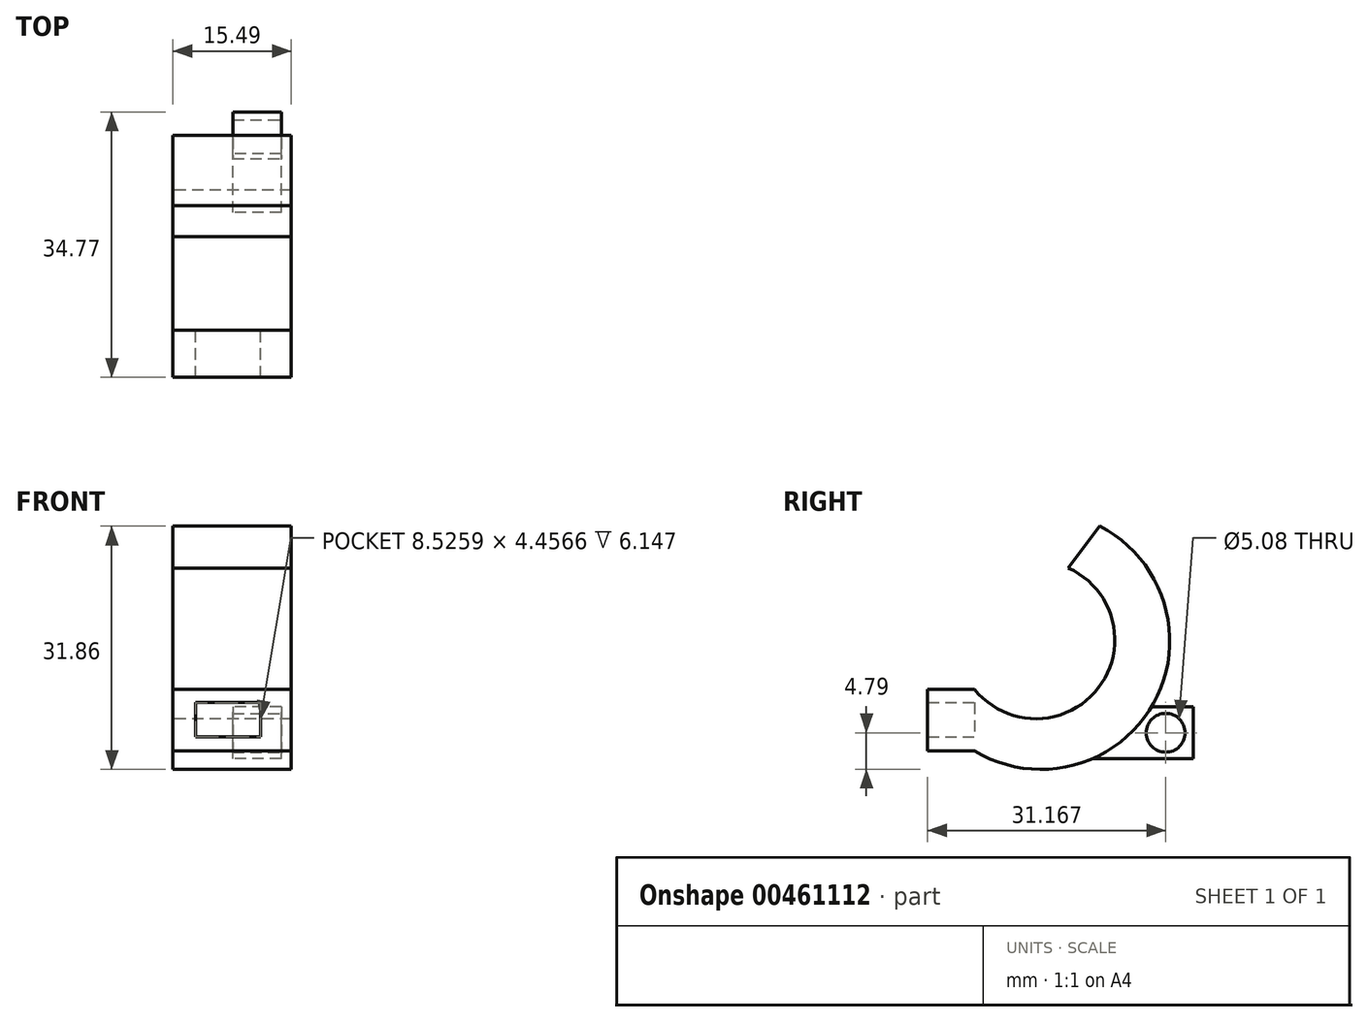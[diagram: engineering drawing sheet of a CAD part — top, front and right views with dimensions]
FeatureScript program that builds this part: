
annotation { "Feature Type Name" : "Feature", "Feature Type Description" : "" }
export const myFeature = defineFeature(function(context is Context, id is Id, definition is map)
    precondition{}
    {
        {
            var Q0;
            Q0=qCreatedBy(makeId("Right.planeOp"),FACE);
            var sketch = newSketch(context, id + "F0", { "sketchPlane" : qUnion([Q0])});
            skArc(sketch, "E0", {"start": v(-28.62, 0) * mm, "mid": v(-12.42, 0.2) * mm, "end": v(-16.36, 15.92) * mm});
            skArc(sketch, "E1", {"start": v(-28.62, -8.04) * mm, "mid": v(-5.19, -1.8) * mm, "end": v(-12.27, 21.4) * mm});
            skLineSegment(sketch, "E2", {"start": v(-16.36, 15.92) * mm, "end": v(-12.27, 21.4) * mm});
            skLineSegment(sketch, "E3", {"start": v(-28.62, 0) * mm, "end": v(-28.62, -8.04) * mm});
            skSolve(sketch);
        }
        {
            var Q0;
            Q0=makeQuery(id+"F0.imprint","IMPRINT",FACE,{"disambiguationData":[TD([[makeQuery(id+"F0.imprint","IMPRINT",EDGE,{"derivedFrom":sQuery(id+"F0.wireOp",EDGE,"E0")}),-1.0]])]});
            extrude(context, id + "F1", {"entities" : qUnion([Q0]), "depth" : 15.5 * mm});
        }
        {
            var Q0;
            Q0=qCreatedBy(makeId("Front.planeOp"),FACE);
            var sketch = newSketch(context, id + "F2", { "sketchPlane" : qUnion([Q0])});
            skLineSegment(sketch, "E4.bottom", {"start": v(7.83, -2.29) * mm, "end": v(14.18, -2.29) * mm});
            skLineSegment(sketch, "E4.top", {"start": v(7.83, -9.05) * mm, "end": v(14.18, -9.05) * mm});
            skLineSegment(sketch, "E4.left", {"start": v(7.83, -2.29) * mm, "end": v(7.83, -9.05) * mm});
            skLineSegment(sketch, "E4.right", {"start": v(14.18, -2.29) * mm, "end": v(14.18, -9.05) * mm});
            skSolve(sketch);
        }
        {
            var Q0;
            Q0=makeQuery(id+"F2.imprint","IMPRINT",FACE,{"disambiguationData":[TD([[makeQuery(id+"F2.imprint","IMPRINT",EDGE,{"derivedFrom":sQuery(id+"F2.wireOp",EDGE,"E4.bottom")}),-1.0]])]});
            extrude(context, id + "F3", {"entities" : qUnion([Q0]), "operationType" : NewBodyOperationType.ADD, "depth" : 13.2 * mm});
        }
        {
            var Q0;
            Q0=makeQuery(id+"F3.opExtrude","SWEPT_FACE",FACE,{"disambiguationData":[OSD([sQuery(id+"F2.wireOp",EDGE,"E4.right")])]});
            var sketch = newSketch(context, id + "F4", { "sketchPlane" : qUnion([Q0])});
            skCircle(sketch, "E5", {"center": v(-3.6, -5.67) * mm, "radius": 2.23 * mm});
            skPoint(sketch, "E5.centerSnap0", {"position": v(0, -5.67) * mm});
            skSolve(sketch);
        }
        {
            var Q0;
            Q0=sQuery(id+"F4.wireOp",VERTEX,"E5.center");
            var Q1;
            Q1=makeQuery(id+"F1.opExtrude","SWEPT_BODY",BODY,{"disambiguationData":[OSD([sQuery(id+"F0.wireOp",EDGE,"E0"),sQuery(id+"F0.wireOp",EDGE,"E1"),sQuery(id+"F0.wireOp",EDGE,"E2"),sQuery(id+"F0.wireOp",EDGE,"E3")])]});
            hole(context, id + "F5", {"style" : HoleStyle.SIMPLE, "endStyle" : HoleEndStyle.THROUGH, "holeDiameter" : 5.08 * mm, "isTappedThrough" : true, "tappedDepth" : 12.7 * mm, "tapClearance" : 3, "locations" : qUnion([Q0]), "scope" : qUnion([Q1])});
        }
        {
            var Q0;
            Q0=makeQuery(id+"F1.opExtrude","SWEPT_FACE",FACE,{"disambiguationData":[OSD([sQuery(id+"F0.wireOp",EDGE,"E3")])]});
            var sketch = newSketch(context, id + "F6", { "sketchPlane" : qUnion([Q0])});
            skLineSegment(sketch, "E6.bottom", {"start": v(11.48, -1.72) * mm, "end": v(2.95, -1.72) * mm});
            skLineSegment(sketch, "E6.top", {"start": v(11.48, -6.18) * mm, "end": v(2.95, -6.18) * mm});
            skLineSegment(sketch, "E6.left", {"start": v(11.48, -1.72) * mm, "end": v(11.48, -6.18) * mm});
            skLineSegment(sketch, "E6.right", {"start": v(2.95, -1.72) * mm, "end": v(2.95, -6.18) * mm});
            skSolve(sketch);
        }
        {
            var Q0;
            Q0=makeQuery(id+"F6.imprint","IMPRINT",FACE,{"disambiguationData":[TD([[makeQuery(id+"F6.imprint","IMPRINT",EDGE,{"derivedFrom":sQuery(id+"F6.wireOp",EDGE,"E6.bottom")}),-1.0]])]});
            extrude(context, id + "F7", {"entities" : qUnion([Q0]), "operationType" : NewBodyOperationType.ADD, "depth" : 6.15 * mm});
        }
    });
